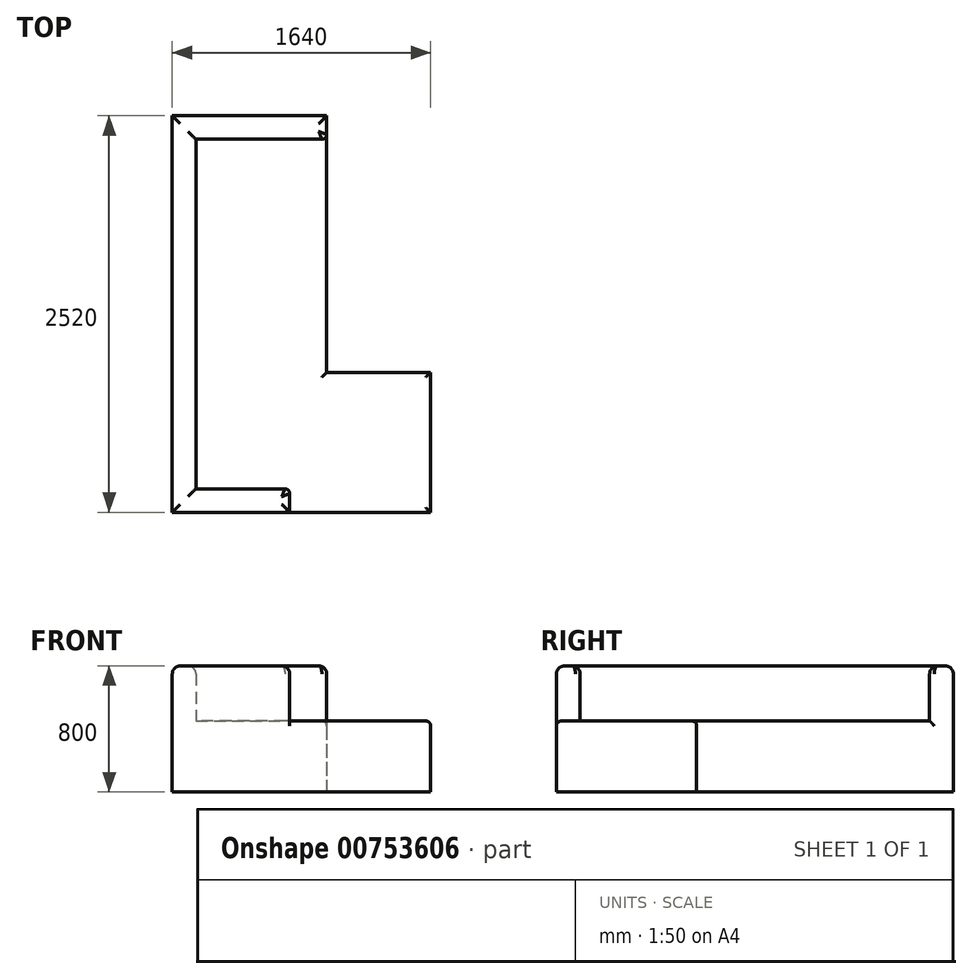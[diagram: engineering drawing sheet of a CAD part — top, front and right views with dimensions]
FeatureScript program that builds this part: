
annotation { "Feature Type Name" : "Feature", "Feature Type Description" : "" }
export const myFeature = defineFeature(function(context is Context, id is Id, definition is map)
    precondition{}
    {
        {
            var Q0;
            Q0=qCreatedBy(makeId("Top.planeOp"),FACE);
            var sketch = newSketch(context, id + "F0", { "sketchPlane" : qUnion([Q0])});
            skLineSegment(sketch, "E0", {"start": v(0, 2520) * mm, "end": v(980, 2520) * mm});
            skLineSegment(sketch, "E1", {"start": v(980, 890) * mm, "end": v(980, 2520) * mm});
            skLineSegment(sketch, "E2", {"start": v(980, 890) * mm, "end": v(1640, 890) * mm});
            skLineSegment(sketch, "E3", {"start": v(1640, 0) * mm, "end": v(1640, 890) * mm});
            skLineSegment(sketch, "E4", {"start": v(1640, 0) * mm, "end": v(0, 0) * mm});
            skLineSegment(sketch, "E5", {"start": v(0, 2520) * mm, "end": v(0, 0) * mm});
            skSolve(sketch);
        }
        {
            var Q0;
            Q0=makeQuery(id+"F0.imprint","IMPRINT",FACE,{"disambiguationData":[TD([[makeQuery(id+"F0.imprint","IMPRINT",EDGE,{"derivedFrom":sQuery(id+"F0.wireOp",EDGE,"E0")}),-1.0]])]});
            extrude(context, id + "F1", {"entities" : qUnion([Q0]), "depth" : 450 * mm, "offsetDistance" : 25 * mm});
        }
        {
            var Q0;
            Q0=makeQuery(id+"F1.opExtrude","CAP_FACE",FACE,{"disambiguationData":[OSD([sQuery(id+"F0.wireOp",EDGE,"E0"),sQuery(id+"F0.wireOp",EDGE,"E1"),sQuery(id+"F0.wireOp",EDGE,"E2"),sQuery(id+"F0.wireOp",EDGE,"E3"),sQuery(id+"F0.wireOp",EDGE,"E4"),sQuery(id+"F0.wireOp",EDGE,"E5")])],"isStart":false});
            var sketch = newSketch(context, id + "F2", { "sketchPlane" : qUnion([Q0])});
            skLineSegment(sketch, "E6", {"start": v(980, 2370) * mm, "end": v(980, 2520) * mm});
            skLineSegment(sketch, "E7", {"start": v(980, 2370) * mm, "end": v(150, 2370) * mm});
            skLineSegment(sketch, "E8", {"start": v(150, 150) * mm, "end": v(150, 2370) * mm});
            skLineSegment(sketch, "E9", {"start": v(150, 150) * mm, "end": v(745, 150) * mm});
            skLineSegment(sketch, "E10", {"start": v(745, 0) * mm, "end": v(745, 150) * mm});
            skLineSegment(sketch, "E11", {"start": v(745, 0) * mm, "end": v(0, 0) * mm});
            skLineSegment(sketch, "E12", {"start": v(0, 2520) * mm, "end": v(0, 0) * mm});
            skLineSegment(sketch, "E13", {"start": v(0, 2520) * mm, "end": v(980, 2520) * mm});
            skSolve(sketch);
        }
        {
            var Q0;
            Q0=makeQuery(id+"F2.imprint","IMPRINT",FACE,{"disambiguationData":[TD([[makeQuery(id+"F2.imprint","IMPRINT",EDGE,{"derivedFrom":sQuery(id+"F2.wireOp",EDGE,"E6")}),1.0]])]});
            extrude(context, id + "F3", {"entities" : qUnion([Q0]), "operationType" : NewBodyOperationType.ADD, "depth" : 350 * mm, "offsetDistance" : 25 * mm});
        }
        {
            var Q0;
            Q0=makeQuery(id+"F3.opExtrude","CAP_FACE",FACE,{"disambiguationData":[OSD([sQuery(id+"F2.wireOp",EDGE,"E6"),sQuery(id+"F2.wireOp",EDGE,"E7"),sQuery(id+"F2.wireOp",EDGE,"E8"),sQuery(id+"F2.wireOp",EDGE,"E9"),sQuery(id+"F2.wireOp",EDGE,"E10"),sQuery(id+"F2.wireOp",EDGE,"E11"),sQuery(id+"F2.wireOp",EDGE,"E12"),sQuery(id+"F2.wireOp",EDGE,"E13")])],"isStart":false});
            fillet(context, id + "F4", {"entities" : qUnion([Q0]), "tangentPropagation" : true, "radius" : 50 * mm, "defaultsChanged" : false, "vertexSettings" : [], "allowEdgeOverflow" : false});
        }
        {
            var Q0;
            Q0=makeQuery(id+"F3.opExtrude","SWEPT_EDGE",EDGE,{"disambiguationData":[OSD([sQuery(id+"F0.wireOp",EDGE,"E1"),sQuery(id+"F2.wireOp",EDGE,"E6"),sQuery(id+"F2.wireOp",EDGE,"E7")])]});
            var Q1;
            Q1=makeQuery(id+"F1.opExtrude","CAP_EDGE",EDGE,{"disambiguationData":[OSD([sQuery(id+"F0.wireOp",EDGE,"E1")])],"isStart":false});
            var Q2;
            Q2=makeQuery(id+"F1.opExtrude","CAP_EDGE",EDGE,{"disambiguationData":[OSD([sQuery(id+"F0.wireOp",EDGE,"E2")])],"isStart":false});
            var Q3;
            Q3=makeQuery(id+"F1.opExtrude","CAP_EDGE",EDGE,{"disambiguationData":[OSD([sQuery(id+"F0.wireOp",EDGE,"E3")])],"isStart":false});
            var Q4;
            Q4=makeQuery(id+"F1.opExtrude","CAP_EDGE",EDGE,{"disambiguationData":[OSD([sQuery(id+"F0.wireOp",EDGE,"E4")])],"isStart":false});
            var Q5;
            Q5=makeQuery(id+"F3.opExtrude","SWEPT_EDGE",EDGE,{"disambiguationData":[OSD([sQuery(id+"F2.wireOp",EDGE,"E9"),sQuery(id+"F2.wireOp",EDGE,"E10")])]});
            fillet(context, id + "F5", {"entities" : qUnion([Q0, Q1, Q2, Q3, Q4, Q5]), "tangentPropagation" : true, "radius" : 30 * mm, "defaultsChanged" : true, "vertexSettings" : [], "allowEdgeOverflow" : false});
        }
    });
